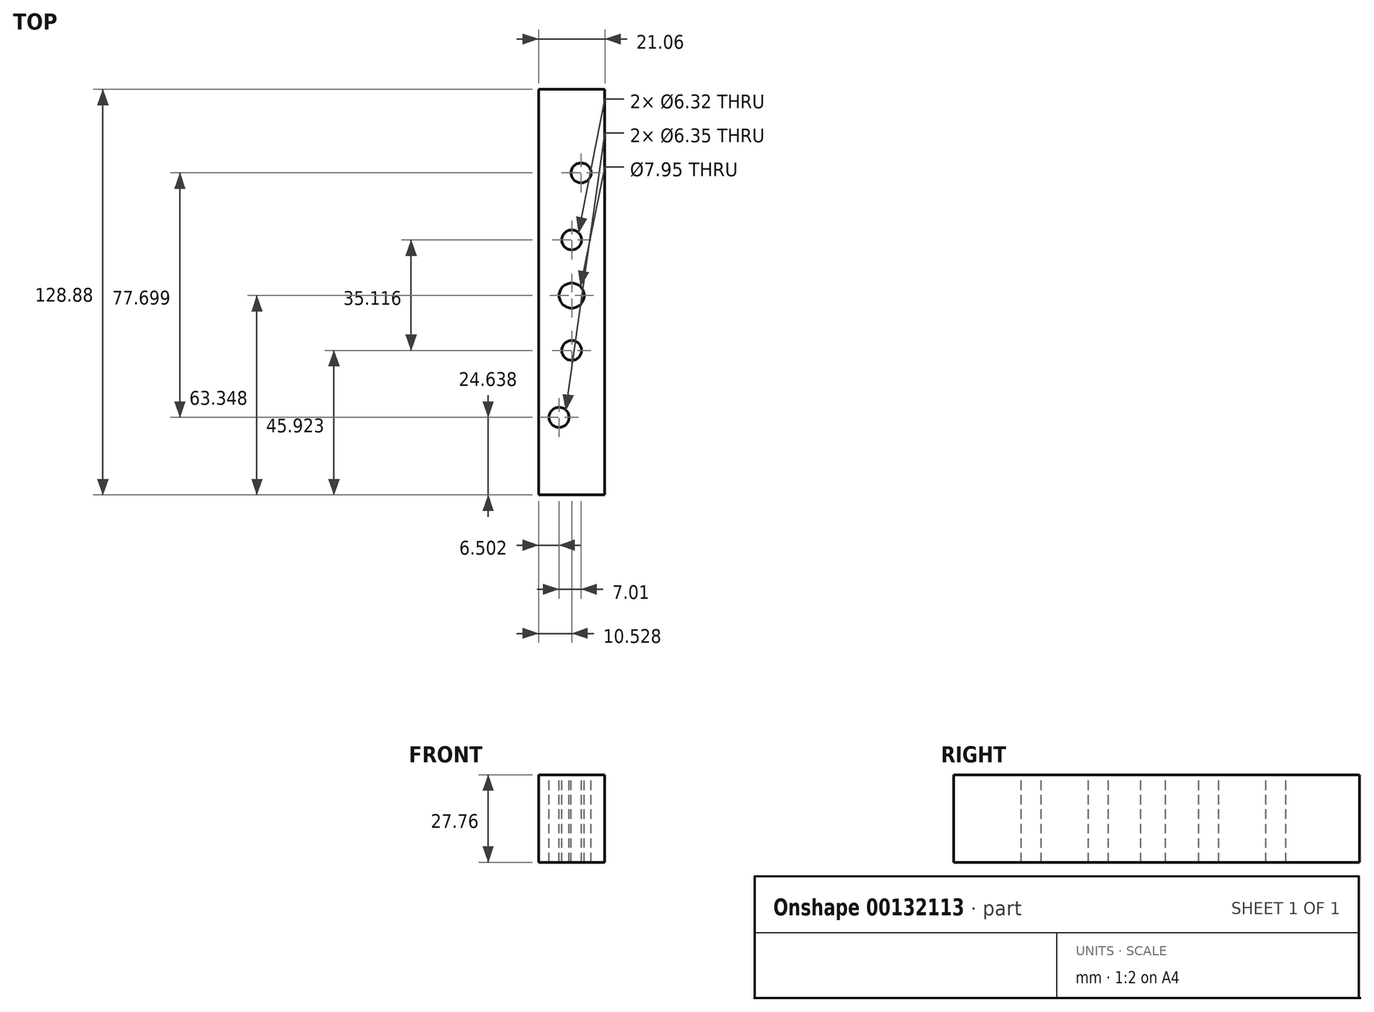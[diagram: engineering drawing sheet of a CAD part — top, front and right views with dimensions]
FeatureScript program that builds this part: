
annotation { "Feature Type Name" : "Feature", "Feature Type Description" : "" }
export const myFeature = defineFeature(function(context is Context, id is Id, definition is map)
    precondition{}
    {
        {
            var Q0;
            Q0=qCreatedBy(makeId("Front.planeOp"),FACE);
            var sketch = newSketch(context, id + "F0", { "sketchPlane" : qUnion([Q0])});
            skLineSegment(sketch, "E0.bottom", {"start": v(0, 0) * mm, "end": v(21.06, 0) * mm});
            skLineSegment(sketch, "E0.top", {"start": v(0, 27.76) * mm, "end": v(21.06, 27.76) * mm});
            skLineSegment(sketch, "E0.left", {"start": v(0, 0) * mm, "end": v(0, 27.76) * mm});
            skLineSegment(sketch, "E0.right", {"start": v(21.06, 0) * mm, "end": v(21.06, 27.76) * mm});
            skSolve(sketch);
        }
        {
            var Q0;
            Q0=qSketchRegion(id+"F0",true);
            extrude(context, id + "F1", {"entities" : qUnion([Q0]), "oppositeDirection" : true, "depth" : 128.88 * mm});
        }
        {
            var Q0;
            Q0=makeQuery(id+"F1.opExtrude","SWEPT_FACE",FACE,{"disambiguationData":[OSD([sQuery(id+"F0.wireOp",EDGE,"E0.top")])]});
            var sketch = newSketch(context, id + "F2", { "sketchPlane" : qUnion([Q0])});
            skCircle(sketch, "E1", {"center": v(10.53, 63.35) * mm, "radius": 3.98 * mm});
            skPoint(sketch, "E1.centerSnap0", {"position": v(10.53, 128.88) * mm});
            skCircle(sketch, "E2", {"center": v(10.53, 45.92) * mm, "radius": 3.16 * mm});
            skCircle(sketch, "E3", {"center": v(10.53, 81.04) * mm, "radius": 3.16 * mm});
            skCircle(sketch, "E4", {"center": v(6.5, 24.64) * mm, "radius": 3.18 * mm});
            skCircle(sketch, "E5", {"center": v(13.51, 102.34) * mm, "radius": 3.18 * mm});
            skLineSegment(sketch, "E6", {"start": v(10.53, 63.35) * mm, "end": v(0, 63.35) * mm});
            skLineSegment(sketch, "E7", {"start": v(10.53, 63.35) * mm, "end": v(21.06, 63.35) * mm});
            skSolve(sketch);
        }
        {
            var Q0;
            Q0=qSketchRegion(id+"F2",true);
            extrude(context, id + "F3", {"entities" : qUnion([Q0]), "operationType" : NewBodyOperationType.REMOVE, "endBound" : BoundingType.THROUGH_ALL, "oppositeDirection" : true, "depth" : 25.4 * mm});
        }
    });
